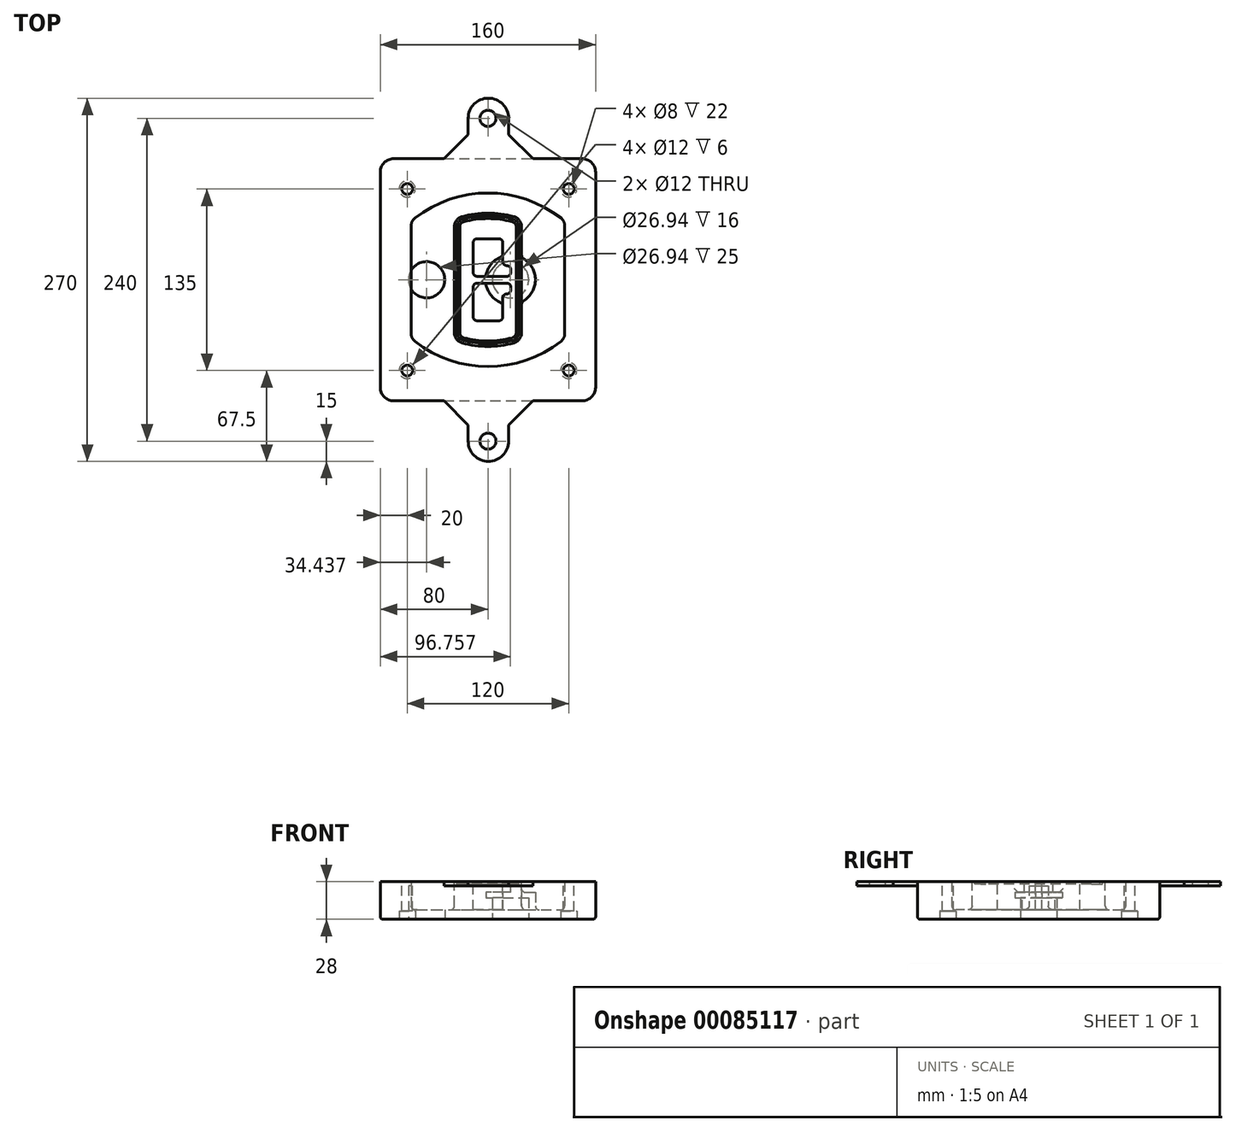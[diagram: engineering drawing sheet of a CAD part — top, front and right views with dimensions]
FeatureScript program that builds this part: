
annotation { "Feature Type Name" : "Feature", "Feature Type Description" : "" }
export const myFeature = defineFeature(function(context is Context, id is Id, definition is map)
    precondition{}
    {
        {
            var Q0;
            Q0=qCreatedBy(makeId("Top.planeOp"),FACE);
            var sketch = newSketch(context, id + "F0", { "sketchPlane" : qUnion([Q0])});
            skPoint(sketch, "E0.rect.middle", {"position": v(0, 0) * mm});
            skLineSegment(sketch, "E1.bottom", {"start": v(-70, -90) * mm, "end": v(70, -90) * mm});
            skLineSegment(sketch, "E1.top", {"start": v(-70, 90) * mm, "end": v(70, 90) * mm});
            skLineSegment(sketch, "E1.left", {"start": v(-80, -80) * mm, "end": v(-80, 80) * mm});
            skLineSegment(sketch, "E1.right", {"start": v(80, -80) * mm, "end": v(80, 80) * mm});
            skLineSegment(sketch, "E2", {"start": v(-80, 90) * mm, "end": v(80, -90) * mm, "construction": true});
            skLineSegment(sketch, "E3", {"start": v(80, 90) * mm, "end": v(-80, -90) * mm, "construction": true});
            skCircle(sketch, "E4", {"center": v(-60, 67.5) * mm, "radius": 4 * mm});
            skCircle(sketch, "E5", {"center": v(60, 67.5) * mm, "radius": 4 * mm});
            skCircle(sketch, "E6", {"center": v(60, -67.5) * mm, "radius": 4 * mm});
            skCircle(sketch, "E7", {"center": v(-60, -67.5) * mm, "radius": 4 * mm});
            skLineSegment(sketch, "E8", {"start": v(-60, 67.5) * mm, "end": v(60, 67.5) * mm, "construction": true});
            skLineSegment(sketch, "E9", {"start": v(60, 67.5) * mm, "end": v(60, -67.5) * mm, "construction": true});
            skLineSegment(sketch, "E10", {"start": v(60, -67.5) * mm, "end": v(-60, -67.5) * mm, "construction": true});
            skLineSegment(sketch, "E11", {"start": v(-60, -67.5) * mm, "end": v(-60, 67.5) * mm, "construction": true});
            skLineSegment(sketch, "E12", {"start": v(-60, 40.3) * mm, "end": v(-60, -40.3) * mm});
            skLineSegment(sketch, "E13", {"start": v(60, 40.3) * mm, "end": v(60, -40.3) * mm});
            skArc(sketch, "E14", {"start": v(56.15, 48.18) * mm, "mid": v(0, 67.5) * mm, "end": v(-56.15, 48.18) * mm});
            skArc(sketch, "E15", {"start": v(-56.15, -48.18) * mm, "mid": v(0, -67.5) * mm, "end": v(56.15, -48.18) * mm});
            skLineSegment(sketch, "E16", {"start": v(-60, 0) * mm, "end": v(60, 0) * mm, "construction": true});
            skPoint(sketch, "E17.visualSharp", {"position": v(-60, -45) * mm});
            skArc(sketch, "E17.filletArc", {"start": v(-60, -40.3) * mm, "mid": v(-58.99, -44.68) * mm, "end": v(-56.15, -48.18) * mm});
            skPoint(sketch, "E18.visualSharp", {"position": v(-60, 45) * mm});
            skArc(sketch, "E18.filletArc", {"start": v(-56.15, 48.18) * mm, "mid": v(-58.99, 44.68) * mm, "end": v(-60, 40.3) * mm});
            skPoint(sketch, "E19.visualSharp", {"position": v(60, 45) * mm});
            skArc(sketch, "E19.filletArc", {"start": v(60, 40.3) * mm, "mid": v(58.99, 44.68) * mm, "end": v(56.15, 48.18) * mm});
            skPoint(sketch, "E20.visualSharp", {"position": v(60, -45) * mm});
            skArc(sketch, "E20.filletArc", {"start": v(56.15, -48.18) * mm, "mid": v(58.99, -44.68) * mm, "end": v(60, -40.3) * mm});
            skPoint(sketch, "E21.visualSharp", {"position": v(-80, 90) * mm});
            skArc(sketch, "E21.filletArc", {"start": v(-70, 90) * mm, "mid": v(-77.07, 87.07) * mm, "end": v(-80, 80) * mm});
            skPoint(sketch, "E22.visualSharp", {"position": v(80, 90) * mm});
            skArc(sketch, "E22.filletArc", {"start": v(80, 80) * mm, "mid": v(77.07, 87.07) * mm, "end": v(70, 90) * mm});
            skPoint(sketch, "E23.visualSharp", {"position": v(80, -90) * mm});
            skArc(sketch, "E23.filletArc", {"start": v(70, -90) * mm, "mid": v(77.07, -87.07) * mm, "end": v(80, -80) * mm});
            skPoint(sketch, "E24.visualSharp", {"position": v(-80, -90) * mm});
            skArc(sketch, "E24.filletArc", {"start": v(-80, -80) * mm, "mid": v(-77.07, -87.07) * mm, "end": v(-70, -90) * mm});
            skArc(sketch, "E25.0", {"start": v(57, 40.3) * mm, "mid": v(56.3, 43.36) * mm, "end": v(54.3, 45.81) * mm});
            skLineSegment(sketch, "E25.1", {"start": v(57, 40.3) * mm, "end": v(57, -40.3) * mm});
            skArc(sketch, "E25.2", {"start": v(54.3, -45.81) * mm, "mid": v(56.3, -43.36) * mm, "end": v(57, -40.3) * mm});
            skArc(sketch, "E25.3", {"start": v(-54.3, -45.81) * mm, "mid": v(0, -64.5) * mm, "end": v(54.3, -45.81) * mm});
            skArc(sketch, "E25.4", {"start": v(-57, -40.3) * mm, "mid": v(-56.3, -43.36) * mm, "end": v(-54.3, -45.81) * mm});
            skArc(sketch, "E25.5", {"start": v(54.3, 45.81) * mm, "mid": v(0, 64.5) * mm, "end": v(-54.3, 45.81) * mm});
            skLineSegment(sketch, "E25.6", {"start": v(-57, 40.3) * mm, "end": v(-57, -40.3) * mm});
            skArc(sketch, "E25.7", {"start": v(-54.3, 45.81) * mm, "mid": v(-56.3, 43.36) * mm, "end": v(-57, 40.3) * mm});
            skArc(sketch, "E26.0", {"start": v(-58.62, 51.33) * mm, "mid": v(-62.58, 46.43) * mm, "end": v(-64, 40.3) * mm});
            skArc(sketch, "E26.1", {"start": v(58.62, 51.33) * mm, "mid": v(0, 71.5) * mm, "end": v(-58.62, 51.33) * mm});
            skArc(sketch, "E26.2", {"start": v(64, 40.3) * mm, "mid": v(62.58, 46.43) * mm, "end": v(58.62, 51.33) * mm});
            skLineSegment(sketch, "E26.3", {"start": v(64, 40.3) * mm, "end": v(64, -40.3) * mm});
            skArc(sketch, "E26.4", {"start": v(58.62, -51.33) * mm, "mid": v(62.58, -46.43) * mm, "end": v(64, -40.3) * mm});
            skLineSegment(sketch, "E26.5", {"start": v(-64, 40.3) * mm, "end": v(-64, -40.3) * mm});
            skArc(sketch, "E26.6", {"start": v(-58.62, -51.33) * mm, "mid": v(0, -71.5) * mm, "end": v(58.62, -51.33) * mm});
            skArc(sketch, "E26.7", {"start": v(-64, -40.3) * mm, "mid": v(-62.58, -46.43) * mm, "end": v(-58.62, -51.33) * mm});
            skSolve(sketch);
        }
        {
            var Q0;
            Q0=makeQuery(id+"F0.imprint","IMPRINT",FACE,{"disambiguationData":[TD([[makeQuery(id+"F0.imprint","IMPRINT",EDGE,{"derivedFrom":sQuery(id+"F0.wireOp",EDGE,"E1.bottom")}),1.0]])]});
            var Q1;
            Q1=makeQuery(id+"F0.imprint","IMPRINT",FACE,{"disambiguationData":[TD([[makeQuery(id+"F0.imprint","IMPRINT",EDGE,{"derivedFrom":sQuery(id+"F0.wireOp",EDGE,"E12")}),1.0]])]});
            var Q2;
            Q2=makeQuery(id+"F0.imprint","IMPRINT",FACE,{"disambiguationData":[TD([[makeQuery(id+"F0.imprint","IMPRINT",EDGE,{"derivedFrom":sQuery(id+"F0.wireOp",EDGE,"E25.0")}),1.0]])]});
            var Q3;
            Q3=makeQuery(id+"F0.imprint","IMPRINT",FACE,{"disambiguationData":[TD([[makeQuery(id+"F0.imprint","IMPRINT",EDGE,{"derivedFrom":sQuery(id+"F0.wireOp",EDGE,"E12")}),-1.0]])]});
            extrude(context, id + "F1", {"entities" : qUnion([Q0, Q1, Q2, Q3]), "oppositeDirection" : true, "depth" : 25 * mm});
        }
        {
            var Q0;
            Q0=makeQuery(id+"F0.imprint","IMPRINT",FACE,{"disambiguationData":[TD([[makeQuery(id+"F0.imprint","IMPRINT",EDGE,{"derivedFrom":sQuery(id+"F0.wireOp",EDGE,"E12")}),1.0]])]});
            extrude(context, id + "F2", {"entities" : qUnion([Q0]), "operationType" : NewBodyOperationType.ADD, "depth" : 3 * mm});
        }
        {
            var Q0;
            Q0=makeQuery(id+"F0.imprint","IMPRINT",FACE,{"disambiguationData":[TD([[makeQuery(id+"F0.imprint","IMPRINT",EDGE,{"derivedFrom":sQuery(id+"F0.wireOp",EDGE,"E25.0")}),1.0]])]});
            extrude(context, id + "F3", {"entities" : qUnion([Q0]), "operationType" : NewBodyOperationType.REMOVE, "oppositeDirection" : true, "depth" : 18 * mm});
        }
        {
            var Q0;
            Q0=makeQuery(id+"F2.opExtrude","CAP_FACE",FACE,{"disambiguationData":[OSD([sQuery(id+"F0.wireOp",EDGE,"E12"),sQuery(id+"F0.wireOp",EDGE,"E13"),sQuery(id+"F0.wireOp",EDGE,"E14"),sQuery(id+"F0.wireOp",EDGE,"E15"),sQuery(id+"F0.wireOp",EDGE,"E17.filletArc"),sQuery(id+"F0.wireOp",EDGE,"E18.filletArc"),sQuery(id+"F0.wireOp",EDGE,"E19.filletArc"),sQuery(id+"F0.wireOp",EDGE,"E20.filletArc"),sQuery(id+"F0.wireOp",EDGE,"E25.0"),sQuery(id+"F0.wireOp",EDGE,"E25.1"),sQuery(id+"F0.wireOp",EDGE,"E25.2"),sQuery(id+"F0.wireOp",EDGE,"E25.3"),sQuery(id+"F0.wireOp",EDGE,"E25.4"),sQuery(id+"F0.wireOp",EDGE,"E25.5"),sQuery(id+"F0.wireOp",EDGE,"E25.6"),sQuery(id+"F0.wireOp",EDGE,"E25.7")])],"isStart":false});
            var sketch = newSketch(context, id + "F4", { "sketchPlane" : qUnion([Q0])});
            skArc(sketch, "E27.0", {"start": v(-19.08, -46.97) * mm, "mid": v(0, -49.5) * mm, "end": v(19.08, -46.97) * mm});
            skArc(sketch, "E28.0", {"start": v(19.08, 46.97) * mm, "mid": v(0, 49.5) * mm, "end": v(-19.08, 46.97) * mm});
            skLineSegment(sketch, "E29", {"start": v(-25, 39.25) * mm, "end": v(-25, -39.25) * mm});
            skLineSegment(sketch, "E30", {"start": v(25, 39.25) * mm, "end": v(25, -39.25) * mm});
            skLineSegment(sketch, "E31", {"start": v(-25, 45.1) * mm, "end": v(25, 45.1) * mm, "construction": true});
            skLineSegment(sketch, "E32", {"start": v(-25, -45.1) * mm, "end": v(25, -45.1) * mm, "construction": true});
            skPoint(sketch, "E33.visualSharp", {"position": v(-25, 45.1) * mm});
            skArc(sketch, "E33.filletArc", {"start": v(-19.08, 46.97) * mm, "mid": v(-23.35, 44.11) * mm, "end": v(-25, 39.25) * mm});
            skPoint(sketch, "E34.visualSharp", {"position": v(25, 45.1) * mm});
            skArc(sketch, "E34.filletArc", {"start": v(25, 39.25) * mm, "mid": v(23.35, 44.11) * mm, "end": v(19.08, 46.97) * mm});
            skPoint(sketch, "E35.visualSharp", {"position": v(25, -45.1) * mm});
            skArc(sketch, "E35.filletArc", {"start": v(19.08, -46.97) * mm, "mid": v(23.35, -44.11) * mm, "end": v(25, -39.25) * mm});
            skPoint(sketch, "E36.visualSharp", {"position": v(-25, -45.1) * mm});
            skArc(sketch, "E36.filletArc", {"start": v(-25, -39.25) * mm, "mid": v(-23.35, -44.11) * mm, "end": v(-19.08, -46.97) * mm});
            skArc(sketch, "E37.0", {"start": v(54.3, 45.81) * mm, "mid": v(0, 64.5) * mm, "end": v(-54.3, 45.81) * mm});
            skArc(sketch, "E37.1", {"start": v(-54.3, 45.81) * mm, "mid": v(-56.3, 43.36) * mm, "end": v(-57, 40.3) * mm});
            skLineSegment(sketch, "E37.2", {"start": v(-57, 40.3) * mm, "end": v(-57, -40.3) * mm});
            skArc(sketch, "E37.3", {"start": v(-57, -40.3) * mm, "mid": v(-56.3, -43.36) * mm, "end": v(-54.3, -45.81) * mm});
            skArc(sketch, "E37.4", {"start": v(-54.3, -45.81) * mm, "mid": v(0, -64.5) * mm, "end": v(54.3, -45.81) * mm});
            skArc(sketch, "E37.5", {"start": v(54.3, -45.81) * mm, "mid": v(56.3, -43.36) * mm, "end": v(57, -40.3) * mm});
            skLineSegment(sketch, "E37.6", {"start": v(57, 40.3) * mm, "end": v(57, -40.3) * mm});
            skArc(sketch, "E37.7", {"start": v(57, 40.3) * mm, "mid": v(56.3, 43.36) * mm, "end": v(54.3, 45.81) * mm});
            skLineSegment(sketch, "E38.0", {"start": v(23, 39.25) * mm, "end": v(23, -39.25) * mm});
            skArc(sketch, "E38.1", {"start": v(18.56, -45.04) * mm, "mid": v(21.76, -42.9) * mm, "end": v(23, -39.25) * mm});
            skArc(sketch, "E38.2", {"start": v(-18.56, -45.04) * mm, "mid": v(0, -47.5) * mm, "end": v(18.56, -45.04) * mm});
            skArc(sketch, "E38.3", {"start": v(-23, -39.25) * mm, "mid": v(-21.76, -42.9) * mm, "end": v(-18.56, -45.04) * mm});
            skLineSegment(sketch, "E38.4", {"start": v(-23, 39.25) * mm, "end": v(-23, -39.25) * mm});
            skArc(sketch, "E38.5", {"start": v(23, 39.25) * mm, "mid": v(21.76, 42.9) * mm, "end": v(18.56, 45.04) * mm});
            skArc(sketch, "E38.6", {"start": v(-18.56, 45.04) * mm, "mid": v(-21.76, 42.9) * mm, "end": v(-23, 39.25) * mm});
            skArc(sketch, "E38.7", {"start": v(18.56, 45.04) * mm, "mid": v(0, 47.5) * mm, "end": v(-18.56, 45.04) * mm});
            skArc(sketch, "E39.0", {"start": v(21, 39.25) * mm, "mid": v(20.18, 41.68) * mm, "end": v(18.04, 43.1) * mm});
            skLineSegment(sketch, "E39.1", {"start": v(21, 39.25) * mm, "end": v(21, -39.25) * mm});
            skArc(sketch, "E39.2", {"start": v(18.04, -43.1) * mm, "mid": v(20.18, -41.68) * mm, "end": v(21, -39.25) * mm});
            skArc(sketch, "E39.3", {"start": v(-18.04, -43.1) * mm, "mid": v(0, -45.5) * mm, "end": v(18.04, -43.1) * mm});
            skArc(sketch, "E39.4", {"start": v(-21, -39.25) * mm, "mid": v(-20.18, -41.68) * mm, "end": v(-18.04, -43.1) * mm});
            skArc(sketch, "E39.5", {"start": v(18.04, 43.1) * mm, "mid": v(0, 45.5) * mm, "end": v(-18.04, 43.1) * mm});
            skLineSegment(sketch, "E39.6", {"start": v(-21, 39.25) * mm, "end": v(-21, -39.25) * mm});
            skArc(sketch, "E39.7", {"start": v(-18.04, 43.1) * mm, "mid": v(-20.18, 41.68) * mm, "end": v(-21, 39.25) * mm});
            skLineSegment(sketch, "E40", {"start": v(-25, 0) * mm, "end": v(25, 0) * mm, "construction": true});
            skLineSegment(sketch, "E41", {"start": v(-11, 5.5) * mm, "end": v(-11, 27.5) * mm});
            skLineSegment(sketch, "E42", {"start": v(-8, 30.5) * mm, "end": v(8, 30.5) * mm});
            skLineSegment(sketch, "E43", {"start": v(11, 27.5) * mm, "end": v(11, 13.5) * mm});
            skLineSegment(sketch, "E44", {"start": v(14, 10.5) * mm, "end": v(14, 10.5) * mm});
            skLineSegment(sketch, "E45", {"start": v(17, 7.5) * mm, "end": v(17, 5.5) * mm});
            skLineSegment(sketch, "E46", {"start": v(14, 2.5) * mm, "end": v(-8, 2.5) * mm});
            skPoint(sketch, "E47.visualSharp", {"position": v(-11, 30.5) * mm});
            skArc(sketch, "E47.filletArc", {"start": v(-8, 30.5) * mm, "mid": v(-10.12, 29.62) * mm, "end": v(-11, 27.5) * mm});
            skPoint(sketch, "E48.visualSharp", {"position": v(11, 30.5) * mm});
            skArc(sketch, "E48.filletArc", {"start": v(11, 27.5) * mm, "mid": v(10.12, 29.62) * mm, "end": v(8, 30.5) * mm});
            skPoint(sketch, "E49.visualSharp", {"position": v(11, 10.5) * mm});
            skArc(sketch, "E49.filletArc", {"start": v(11, 13.5) * mm, "mid": v(11.88, 11.38) * mm, "end": v(14, 10.5) * mm});
            skPoint(sketch, "E50.visualSharp", {"position": v(17, 10.5) * mm});
            skArc(sketch, "E50.filletArc", {"start": v(17, 7.5) * mm, "mid": v(16.12, 9.62) * mm, "end": v(14, 10.5) * mm});
            skPoint(sketch, "E51.visualSharp", {"position": v(17, 2.5) * mm});
            skArc(sketch, "E51.filletArc", {"start": v(14, 2.5) * mm, "mid": v(16.12, 3.38) * mm, "end": v(17, 5.5) * mm});
            skPoint(sketch, "E52.visualSharp", {"position": v(-11, 2.5) * mm});
            skArc(sketch, "E52.filletArc", {"start": v(-11, 5.5) * mm, "mid": v(-10.12, 3.38) * mm, "end": v(-8, 2.5) * mm});
            skLineSegment(sketch, "E53.0.MirrorCS", {"start": v(14, -2.5) * mm, "end": v(-8, -2.5) * mm});
            skArc(sketch, "E54.0.MirrorCS", {"start": v(-11, -5.5) * mm, "mid": v(-10.12, -3.38) * mm, "end": v(-8, -2.5) * mm});
            skLineSegment(sketch, "E55.0.MirrorCS", {"start": v(-11, -5.5) * mm, "end": v(-11, -27.5) * mm});
            skArc(sketch, "E56.0.MirrorCS", {"start": v(-8, -30.5) * mm, "mid": v(-10.12, -29.62) * mm, "end": v(-11, -27.5) * mm});
            skLineSegment(sketch, "E57.0.MirrorCS", {"start": v(-8, -30.5) * mm, "end": v(8, -30.5) * mm});
            skArc(sketch, "E58.0.MirrorCS", {"start": v(11, -27.5) * mm, "mid": v(10.12, -29.62) * mm, "end": v(8, -30.5) * mm});
            skLineSegment(sketch, "E59.0.MirrorCS", {"start": v(11, -27.5) * mm, "end": v(11, -13.5) * mm});
            skArc(sketch, "E60.0.MirrorCS", {"start": v(11, -13.5) * mm, "mid": v(11.88, -11.38) * mm, "end": v(14, -10.5) * mm});
            skArc(sketch, "E61.0.MirrorCS", {"start": v(17, -7.5) * mm, "mid": v(16.12, -9.62) * mm, "end": v(14, -10.5) * mm});
            skLineSegment(sketch, "E62.0.MirrorCS", {"start": v(17, -7.5) * mm, "end": v(17, -5.5) * mm});
            skArc(sketch, "E63.0.MirrorCS", {"start": v(14, -2.5) * mm, "mid": v(16.12, -3.38) * mm, "end": v(17, -5.5) * mm});
            skSolve(sketch);
        }
        {
            var Q0;
            Q0=makeQuery(id+"F4.imprint","IMPRINT",FACE,{"disambiguationData":[TD([[makeQuery(id+"F4.imprint","IMPRINT",EDGE,{"derivedFrom":sQuery(id+"F4.wireOp",EDGE,"E27.0")}),1.0]])]});
            var Q1;
            Q1=makeQuery(id+"F4.imprint","IMPRINT",FACE,{"disambiguationData":[TD([[makeQuery(id+"F4.imprint","IMPRINT",EDGE,{"derivedFrom":sQuery(id+"F4.wireOp",EDGE,"E38.0")}),-1.0]])]});
            var Q2;
            Q2=makeQuery(id+"F4.imprint","IMPRINT",FACE,{"disambiguationData":[TD([[makeQuery(id+"F4.imprint","IMPRINT",EDGE,{"derivedFrom":sQuery(id+"F4.wireOp",EDGE,"E39.0")}),1.0]])]});
            extrude(context, id + "F5", {"entities" : qUnion([Q0, Q1, Q2]), "operationType" : NewBodyOperationType.ADD, "endBound" : BoundingType.UP_TO_NEXT, "oppositeDirection" : true, "depth" : 25 * mm});
        }
        {
            var Q0;
            Q0=makeQuery(id+"F4.imprint","IMPRINT",FACE,{"disambiguationData":[TD([[makeQuery(id+"F4.imprint","IMPRINT",EDGE,{"derivedFrom":sQuery(id+"F4.wireOp",EDGE,"E38.0")}),-1.0]])]});
            extrude(context, id + "F6", {"entities" : qUnion([Q0]), "operationType" : NewBodyOperationType.REMOVE, "oppositeDirection" : true, "depth" : 2 * mm});
        }
        {
            var Q0;
            Q0=makeQuery(id+"F1.opExtrude","CAP_FACE",FACE,{"disambiguationData":[OSD([sQuery(id+"F0.wireOp",EDGE,"E1.bottom"),sQuery(id+"F0.wireOp",EDGE,"E1.top"),sQuery(id+"F0.wireOp",EDGE,"E1.left"),sQuery(id+"F0.wireOp",EDGE,"E1.right"),sQuery(id+"F0.wireOp",EDGE,"E4"),sQuery(id+"F0.wireOp",EDGE,"E5"),sQuery(id+"F0.wireOp",EDGE,"E6"),sQuery(id+"F0.wireOp",EDGE,"E7"),sQuery(id+"F0.wireOp",EDGE,"E21.filletArc"),sQuery(id+"F0.wireOp",EDGE,"E22.filletArc"),sQuery(id+"F0.wireOp",EDGE,"E23.filletArc"),sQuery(id+"F0.wireOp",EDGE,"E24.filletArc")])],"isStart":false});
            var sketch = newSketch(context, id + "F7", { "sketchPlane" : qUnion([Q0])});
            skCircle(sketch, "E64", {"center": v(16.76, 0) * mm, "radius": 13.47 * mm});
            skCircle(sketch, "E65", {"center": v(-45.56, 0) * mm, "radius": 13.47 * mm});
            skLineSegment(sketch, "E66", {"start": v(80, 0) * mm, "end": v(-80, 0) * mm});
            skCircle(sketch, "E67", {"center": v(16.76, 0) * mm, "radius": 18.47 * mm});
            skCircle(sketch, "E68", {"center": v(60, -67.5) * mm, "radius": 6 * mm});
            skCircle(sketch, "E69", {"center": v(-60, -67.5) * mm, "radius": 6 * mm});
            skCircle(sketch, "E70", {"center": v(-60, 67.5) * mm, "radius": 6 * mm});
            skCircle(sketch, "E71", {"center": v(60, 67.5) * mm, "radius": 6 * mm});
            skSolve(sketch);
        }
        {
            var Q0;
            {var subQ1=sQuery(id+"F7.wireOp",EDGE,"E66");var subQ4=sQuery(id+"F7.wireOp",EDGE,"E64");var subQ6=makeQuery(id+"F7.imprint","INTERSECT",VERTEX,{"disambiguationData":[OD(0.0)],"derivedFrom":[subQ4,subQ1]});Q0=makeQuery(id+"F7.imprint","IMPRINT",FACE,{"disambiguationData":[TD([[makeQuery(id+"F7.imprint","IMPRINT",EDGE,{"disambiguationData":[TD([[subQ6,-1.0]])],"derivedFrom":subQ4}),-1.0]])]});}
            var Q1;
            {var subQ0=sQuery(id+"F7.wireOp",EDGE,"E66");var subQ1=sQuery(id+"F7.wireOp",EDGE,"E64");var subQ3=makeQuery(id+"F7.imprint","INTERSECT",VERTEX,{"disambiguationData":[OD(0.0)],"derivedFrom":[subQ1,subQ0]});Q1=makeQuery(id+"F7.imprint","IMPRINT",FACE,{"disambiguationData":[TD([[makeQuery(id+"F7.imprint","IMPRINT",EDGE,{"disambiguationData":[TD([[subQ3,-1.0]])],"derivedFrom":subQ1}),1.0]])]});}
            var Q2;
            {var subQ0=sQuery(id+"F7.wireOp",EDGE,"E66");var subQ1=sQuery(id+"F7.wireOp",EDGE,"E64");var subQ3=makeQuery(id+"F7.imprint","INTERSECT",VERTEX,{"disambiguationData":[OD(0.0)],"derivedFrom":[subQ1,subQ0]});Q2=makeQuery(id+"F7.imprint","IMPRINT",FACE,{"disambiguationData":[TD([[makeQuery(id+"F7.imprint","IMPRINT",EDGE,{"disambiguationData":[TD([[subQ3,1.0]])],"derivedFrom":subQ1}),1.0]])]});}
            var Q3;
            {var subQ1=sQuery(id+"F7.wireOp",EDGE,"E66");var subQ4=sQuery(id+"F7.wireOp",EDGE,"E64");var subQ6=makeQuery(id+"F7.imprint","INTERSECT",VERTEX,{"disambiguationData":[OD(0.0)],"derivedFrom":[subQ4,subQ1]});Q3=makeQuery(id+"F7.imprint","IMPRINT",FACE,{"disambiguationData":[TD([[makeQuery(id+"F7.imprint","IMPRINT",EDGE,{"disambiguationData":[TD([[subQ6,1.0]])],"derivedFrom":subQ4}),-1.0]])]});}
            extrude(context, id + "F8", {"entities" : qUnion([Q0, Q1, Q2, Q3]), "operationType" : NewBodyOperationType.ADD, "oppositeDirection" : true, "depth" : 20 * mm});
        }
        {
            var Q0;
            {var subQ0=sQuery(id+"F7.wireOp",EDGE,"E66");var subQ1=sQuery(id+"F7.wireOp",EDGE,"E64");var subQ3=makeQuery(id+"F7.imprint","INTERSECT",VERTEX,{"disambiguationData":[OD(0.0)],"derivedFrom":[subQ1,subQ0]});Q0=makeQuery(id+"F7.imprint","IMPRINT",FACE,{"disambiguationData":[TD([[makeQuery(id+"F7.imprint","IMPRINT",EDGE,{"disambiguationData":[TD([[subQ3,-1.0]])],"derivedFrom":subQ1}),1.0]])]});}
            var Q1;
            {var subQ0=sQuery(id+"F7.wireOp",EDGE,"E66");var subQ1=sQuery(id+"F7.wireOp",EDGE,"E64");var subQ3=makeQuery(id+"F7.imprint","INTERSECT",VERTEX,{"disambiguationData":[OD(0.0)],"derivedFrom":[subQ1,subQ0]});Q1=makeQuery(id+"F7.imprint","IMPRINT",FACE,{"disambiguationData":[TD([[makeQuery(id+"F7.imprint","IMPRINT",EDGE,{"disambiguationData":[TD([[subQ3,1.0]])],"derivedFrom":subQ1}),1.0]])]});}
            extrude(context, id + "F9", {"entities" : qUnion([Q0, Q1]), "operationType" : NewBodyOperationType.REMOVE, "oppositeDirection" : true, "depth" : 16 * mm});
        }
        {
            var Q0;
            {var subQ0=sQuery(id+"F7.wireOp",EDGE,"E66");var subQ1=sQuery(id+"F7.wireOp",EDGE,"E65");var subQ3=makeQuery(id+"F7.imprint","INTERSECT",VERTEX,{"disambiguationData":[OD(0.0)],"derivedFrom":[subQ1,subQ0]});Q0=makeQuery(id+"F7.imprint","IMPRINT",FACE,{"disambiguationData":[TD([[makeQuery(id+"F7.imprint","IMPRINT",EDGE,{"disambiguationData":[TD([[subQ3,-1.0]])],"derivedFrom":subQ1}),1.0]])]});}
            var Q1;
            {var subQ0=sQuery(id+"F7.wireOp",EDGE,"E66");var subQ1=sQuery(id+"F7.wireOp",EDGE,"E65");var subQ3=makeQuery(id+"F7.imprint","INTERSECT",VERTEX,{"disambiguationData":[OD(0.0)],"derivedFrom":[subQ1,subQ0]});Q1=makeQuery(id+"F7.imprint","IMPRINT",FACE,{"disambiguationData":[TD([[makeQuery(id+"F7.imprint","IMPRINT",EDGE,{"disambiguationData":[TD([[subQ3,1.0]])],"derivedFrom":subQ1}),1.0]])]});}
            extrude(context, id + "F10", {"entities" : qUnion([Q0, Q1]), "operationType" : NewBodyOperationType.REMOVE, "oppositeDirection" : true, "depth" : 25 * mm});
        }
        {
            var Q0;
            Q0=makeQuery(id+"F7.imprint","IMPRINT",FACE,{"disambiguationData":[TD([[makeQuery(id+"F7.imprint","IMPRINT",EDGE,{"derivedFrom":sQuery(id+"F7.wireOp",EDGE,"E68")}),1.0]])]});
            var Q1;
            Q1=makeQuery(id+"F7.imprint","IMPRINT",FACE,{"disambiguationData":[TD([[makeQuery(id+"F7.imprint","IMPRINT",EDGE,{"derivedFrom":makeQuery(id+"F1.opExtrude","CAP_EDGE",EDGE,{"disambiguationData":[OSD([sQuery(id+"F0.wireOp",EDGE,"E5")])],"isStart":false})}),-1.0]])]});
            var Q2;
            Q2=makeQuery(id+"F7.imprint","IMPRINT",FACE,{"disambiguationData":[TD([[makeQuery(id+"F7.imprint","IMPRINT",EDGE,{"derivedFrom":sQuery(id+"F7.wireOp",EDGE,"E69")}),1.0]])]});
            var Q3;
            Q3=makeQuery(id+"F7.imprint","IMPRINT",FACE,{"disambiguationData":[TD([[makeQuery(id+"F7.imprint","IMPRINT",EDGE,{"derivedFrom":makeQuery(id+"F1.opExtrude","CAP_EDGE",EDGE,{"disambiguationData":[OSD([sQuery(id+"F0.wireOp",EDGE,"E4")])],"isStart":false})}),-1.0]])]});
            var Q4;
            Q4=makeQuery(id+"F7.imprint","IMPRINT",FACE,{"disambiguationData":[TD([[makeQuery(id+"F7.imprint","IMPRINT",EDGE,{"derivedFrom":sQuery(id+"F7.wireOp",EDGE,"E70")}),1.0]])]});
            var Q5;
            Q5=makeQuery(id+"F7.imprint","IMPRINT",FACE,{"disambiguationData":[TD([[makeQuery(id+"F7.imprint","IMPRINT",EDGE,{"derivedFrom":makeQuery(id+"F1.opExtrude","CAP_EDGE",EDGE,{"disambiguationData":[OSD([sQuery(id+"F0.wireOp",EDGE,"E7")])],"isStart":false})}),-1.0]])]});
            var Q6;
            Q6=makeQuery(id+"F7.imprint","IMPRINT",FACE,{"disambiguationData":[TD([[makeQuery(id+"F7.imprint","IMPRINT",EDGE,{"derivedFrom":sQuery(id+"F7.wireOp",EDGE,"E71")}),1.0]])]});
            var Q7;
            Q7=makeQuery(id+"F7.imprint","IMPRINT",FACE,{"disambiguationData":[TD([[makeQuery(id+"F7.imprint","IMPRINT",EDGE,{"derivedFrom":makeQuery(id+"F1.opExtrude","CAP_EDGE",EDGE,{"disambiguationData":[OSD([sQuery(id+"F0.wireOp",EDGE,"E6")])],"isStart":false})}),-1.0]])]});
            extrude(context, id + "F11", {"entities" : qUnion([Q0, Q1, Q2, Q3, Q4, Q5, Q6, Q7]), "operationType" : NewBodyOperationType.REMOVE, "oppositeDirection" : true, "depth" : 6 * mm});
        }
        {
            var Q0;
            Q0=makeQuery(id+"F9.boolean.opBoolean","COPY",FACE,{"derivedFrom":makeQuery(id+"F9.opExtrude","CAP_FACE",FACE,{"disambiguationData":[OSD([sQuery(id+"F7.wireOp",EDGE,"E64")])],"isStart":false})});
            var sketch = newSketch(context, id + "F12", { "sketchPlane" : qUnion([Q0])});
            skArc(sketch, "E72.0", {"start": v(11, 17.55) * mm, "mid": v(2.57, 11.82) * mm, "end": v(-1.54, 2.5) * mm});
            skArc(sketch, "E72.1", {"start": v(-1.54, -2.5) * mm, "mid": v(2.57, -11.82) * mm, "end": v(11, -17.55) * mm});
            skLineSegment(sketch, "E73", {"start": v(-1.54, -2.5) * mm, "end": v(14, -2.5) * mm});
            skLineSegment(sketch, "E74.0", {"start": v(14, 2.5) * mm, "end": v(-1.54, 2.5) * mm});
            skArc(sketch, "E74.1", {"start": v(14, 2.5) * mm, "mid": v(16.12, 3.38) * mm, "end": v(17, 5.5) * mm});
            skLineSegment(sketch, "E74.2", {"start": v(17, 7.5) * mm, "end": v(17, 5.5) * mm});
            skArc(sketch, "E74.3", {"start": v(17, 7.5) * mm, "mid": v(16.12, 9.62) * mm, "end": v(14, 10.5) * mm});
            skArc(sketch, "E74.4", {"start": v(11, 13.5) * mm, "mid": v(11.88, 11.38) * mm, "end": v(14, 10.5) * mm});
            skLineSegment(sketch, "E74.5", {"start": v(11, 17.55) * mm, "end": v(11, 13.5) * mm});
            skLineSegment(sketch, "E74.7", {"start": v(14, -2.5) * mm, "end": v(-1.54, -2.5) * mm});
            skArc(sketch, "E74.8", {"start": v(14, -2.5) * mm, "mid": v(16.12, -3.38) * mm, "end": v(17, -5.5) * mm});
            skLineSegment(sketch, "E74.9", {"start": v(17, -7.5) * mm, "end": v(17, -5.5) * mm});
            skArc(sketch, "E74.10", {"start": v(17, -7.5) * mm, "mid": v(16.12, -9.62) * mm, "end": v(14, -10.5) * mm});
            skArc(sketch, "E74.11", {"start": v(11, -13.5) * mm, "mid": v(11.88, -11.38) * mm, "end": v(14, -10.5) * mm});
            skLineSegment(sketch, "E74.12", {"start": v(11, -17.55) * mm, "end": v(11, -13.5) * mm});
            skPoint(sketch, "E75.orphan", {"position": v(11, -27.5) * mm});
            skPoint(sketch, "E76.orphan", {"position": v(-8, -2.5) * mm});
            skPoint(sketch, "E77.orphan", {"position": v(-8, 2.5) * mm});
            skPoint(sketch, "E78.orphan", {"position": v(11, 27.5) * mm});
            skSolve(sketch);
        }
        {
            var Q0;
            {var subQ7=sQuery(id+"F12.wireOp",EDGE,"E72.0");var subQ14=sQuery(id+"F12.wireOp",EDGE,"E72.1");var subQ16=sQuery(id+"F12.wireOp",EDGE,"E74.1");var subQ18=sQuery(id+"F12.wireOp",EDGE,"E74.8");Q0=qUnion([makeQuery(id+"F12.imprint","IMPRINT",FACE,{"disambiguationData":[TD([[makeQuery(id+"F12.imprint","IMPRINT",EDGE,{"derivedFrom":subQ7}),1.0]])]}),makeQuery(id+"F12.imprint","IMPRINT",FACE,{"disambiguationData":[TD([[makeQuery(id+"F12.imprint","IMPRINT",EDGE,{"derivedFrom":subQ14}),1.0]])]}),makeQuery(id+"F12.imprint","IMPRINT",FACE,{"disambiguationData":[TD([[makeQuery(id+"F12.imprint","IMPRINT",EDGE,{"derivedFrom":subQ16}),1.0]])]}),makeQuery(id+"F12.imprint","IMPRINT",FACE,{"disambiguationData":[TD([[makeQuery(id+"F12.imprint","IMPRINT",EDGE,{"derivedFrom":subQ18}),-1.0]])]})]);}
            var Q1;
            Q1=makeQuery(id+"F5.boolean.opBoolean","SPLIT",FACE,{"disambiguationData":[TD([makeQuery(id+"F5.opExtrude","SWEPT_FACE",FACE,{"disambiguationData":[OSD([sQuery(id+"F4.wireOp",EDGE,"E41")])]})])],"derivedFrom":makeQuery(id+"F3.boolean.opBoolean","COPY",FACE,{"derivedFrom":makeQuery(id+"F3.opExtrude","CAP_FACE",FACE,{"disambiguationData":[OSD([sQuery(id+"F0.wireOp",EDGE,"E25.0"),sQuery(id+"F0.wireOp",EDGE,"E25.1"),sQuery(id+"F0.wireOp",EDGE,"E25.2"),sQuery(id+"F0.wireOp",EDGE,"E25.3"),sQuery(id+"F0.wireOp",EDGE,"E25.4"),sQuery(id+"F0.wireOp",EDGE,"E25.5"),sQuery(id+"F0.wireOp",EDGE,"E25.6"),sQuery(id+"F0.wireOp",EDGE,"E25.7")])],"isStart":false})})});
            extrude(context, id + "F13", {"entities" : qUnion([Q0]), "operationType" : NewBodyOperationType.REMOVE, "endBound" : BoundingType.UP_TO_SURFACE, "endBoundEntityFace" : qUnion([Q1]), "depth" : 25 * mm});
        }
        {
            var Q0;
            Q0=makeQuery(id+"F3.boolean.opBoolean","COPY",EDGE,{"derivedFrom":makeQuery(id+"F3.opExtrude","CAP_EDGE",EDGE,{"disambiguationData":[OSD([sQuery(id+"F0.wireOp",EDGE,"E25.6")])],"isStart":false})});
            var Q1;
            Q1=makeQuery(id+"F8.boolean.opBoolean","INTERSECT",EDGE,{"derivedFrom":[makeQuery(id+"F5.opExtrude","SWEPT_FACE",FACE,{"disambiguationData":[OSD([sQuery(id+"F4.wireOp",EDGE,"E30")])]}),makeQuery(id+"F8.opExtrude","CAP_FACE",FACE,{"disambiguationData":[OSD([sQuery(id+"F7.wireOp",EDGE,"E67")])],"isStart":false})]});
            var Q2;
            Q2=makeQuery(id+"F8.boolean.opBoolean","INTERSECT",EDGE,{"disambiguationData":[OD(1.0)],"derivedFrom":[makeQuery(id+"F5.opExtrude","SWEPT_FACE",FACE,{"disambiguationData":[OSD([sQuery(id+"F4.wireOp",EDGE,"E30")])]}),makeQuery(id+"F8.opExtrude","SWEPT_FACE",FACE,{"disambiguationData":[OSD([sQuery(id+"F7.wireOp",EDGE,"E67")])]})]});
            var Q3;
            {var subQ0=sQuery(id+"F4.wireOp",EDGE,"E30");Q3=makeQuery(id+"F8.boolean.opBoolean","SPLIT",EDGE,{"disambiguationData":[TD([makeQuery(id+"F5.opExtrude","SWEPT_FACE",FACE,{"disambiguationData":[OSD([sQuery(id+"F4.wireOp",EDGE,"E35.filletArc")])]})])],"derivedFrom":makeQuery(id+"F5.opExtrude","CAP_EDGE",EDGE,{"disambiguationData":[OSD([subQ0])],"isStart":false})});}
            var Q4;
            {var subQ0=sQuery(id+"F0.wireOp",EDGE,"E25.7");var subQ1=sQuery(id+"F0.wireOp",EDGE,"E25.1");var subQ2=sQuery(id+"F0.wireOp",EDGE,"E25.6");var subQ3=sQuery(id+"F0.wireOp",EDGE,"E25.5");var subQ4=sQuery(id+"F0.wireOp",EDGE,"E25.4");var subQ5=sQuery(id+"F0.wireOp",EDGE,"E25.0");var subQ6=sQuery(id+"F0.wireOp",EDGE,"E25.2");var subQ7=sQuery(id+"F0.wireOp",EDGE,"E25.3");Q4=makeQuery(id+"F8.boolean.opBoolean","INTERSECT",EDGE,{"derivedFrom":[makeQuery(id+"F5.boolean.opBoolean","SPLIT",FACE,{"disambiguationData":[TD([makeQuery(id+"F2.opExtrude","SWEPT_FACE",FACE,{"disambiguationData":[OSD([subQ5])]})])],"derivedFrom":makeQuery(id+"F3.boolean.opBoolean","COPY",FACE,{"derivedFrom":makeQuery(id+"F3.opExtrude","CAP_FACE",FACE,{"disambiguationData":[OSD([subQ5,subQ1,subQ6,subQ7,subQ4,subQ3,subQ2,subQ0])],"isStart":false})})}),makeQuery(id+"F8.opExtrude","SWEPT_FACE",FACE,{"disambiguationData":[OSD([sQuery(id+"F7.wireOp",EDGE,"E67")])]})]});}
            var Q5;
            Q5=makeQuery(id+"F8.boolean.opBoolean","INTERSECT",EDGE,{"disambiguationData":[OD(0.0)],"derivedFrom":[makeQuery(id+"F5.opExtrude","SWEPT_FACE",FACE,{"disambiguationData":[OSD([sQuery(id+"F4.wireOp",EDGE,"E30")])]}),makeQuery(id+"F8.opExtrude","SWEPT_FACE",FACE,{"disambiguationData":[OSD([sQuery(id+"F7.wireOp",EDGE,"E67")])]})]});
            fillet(context, id + "F14", {"entities" : qUnion([Q0, Q1, Q2, Q3, Q4, Q5]), "radius" : 3 * mm, "tangentPropagation" : true, "allowEdgeOverflow" : false});
        }
        {
            var Q0;
            Q0=makeQuery(id+"F1.opExtrude","CAP_EDGE",EDGE,{"disambiguationData":[OSD([sQuery(id+"F0.wireOp",EDGE,"E1.bottom")])],"isStart":false});
            fillet(context, id + "F15", {"entities" : qUnion([Q0]), "radius" : 2 * mm, "tangentPropagation" : true, "allowEdgeOverflow" : false});
        }
        {
            var Q0;
            {var subQ0=sQuery(id+"F0.wireOp",EDGE,"E22.filletArc");var subQ1=sQuery(id+"F0.wireOp",EDGE,"E7");var subQ2=sQuery(id+"F0.wireOp",EDGE,"E6");var subQ3=sQuery(id+"F0.wireOp",EDGE,"E5");var subQ4=sQuery(id+"F0.wireOp",EDGE,"E4");var subQ5=sQuery(id+"F0.wireOp",EDGE,"E1.bottom");var subQ6=sQuery(id+"F0.wireOp",EDGE,"E21.filletArc");var subQ7=sQuery(id+"F0.wireOp",EDGE,"E1.top");var subQ8=sQuery(id+"F0.wireOp",EDGE,"E1.left");var subQ9=sQuery(id+"F0.wireOp",EDGE,"E1.right");var subQ10=sQuery(id+"F0.wireOp",EDGE,"E23.filletArc");var subQ11=sQuery(id+"F0.wireOp",EDGE,"E24.filletArc");Q0=makeQuery(id+"F2.boolean.opBoolean","SPLIT",FACE,{"disambiguationData":[TD([makeQuery(id+"F1.opExtrude","SWEPT_FACE",FACE,{"disambiguationData":[OSD([subQ5])]})])],"derivedFrom":makeQuery(id+"F1.opExtrude","CAP_FACE",FACE,{"disambiguationData":[OSD([subQ5,subQ7,subQ8,subQ9,subQ4,subQ3,subQ2,subQ1,subQ6,subQ0,subQ10,subQ11])],"isStart":true})});}
            var sketch = newSketch(context, id + "F16", { "sketchPlane" : qUnion([Q0])});
            skLineSegment(sketch, "E79", {"start": v(0, 90) * mm, "end": v(0, 120) * mm, "construction": true});
            skPoint(sketch, "E79.endSnap0", {"position": v(0, 90) * mm});
            skCircle(sketch, "E80", {"center": v(0, 120) * mm, "radius": 6 * mm});
            skLineSegment(sketch, "E81", {"start": v(15.3, 120) * mm, "end": v(15.3, 108) * mm});
            skLineSegment(sketch, "E82", {"start": v(15.3, 108) * mm, "end": v(33.3, 90) * mm});
            skLineSegment(sketch, "E83", {"start": v(-14.7, 120) * mm, "end": v(-14.7, 108) * mm});
            skLineSegment(sketch, "E84", {"start": v(-14.7, 108) * mm, "end": v(-32.7, 90) * mm});
            skArc(sketch, "E85", {"start": v(15.3, 120) * mm, "mid": v(0.3, 135) * mm, "end": v(-14.7, 120) * mm});
            skLineSegment(sketch, "E86", {"start": v(-88.78, 0) * mm, "end": v(126.15, 0) * mm, "construction": true});
            skPoint(sketch, "E86.startSnap0", {"position": v(-80, 0) * mm});
            skPoint(sketch, "E86.endSnap0", {"position": v(-60, 0) * mm});
            skLineSegment(sketch, "E87.MirrorCS", {"start": v(15.3, -120) * mm, "end": v(15.3, -108) * mm});
            skPoint(sketch, "E88.MirrorP", {"position": v(0, -90) * mm});
            skCircle(sketch, "E89.MirrorC", {"center": v(0, -120) * mm, "radius": 6 * mm});
            skLineSegment(sketch, "E90.MirrorCS", {"start": v(-14.7, -120) * mm, "end": v(-14.7, -108) * mm});
            skArc(sketch, "E91.MirrorCS", {"start": v(15.3, -120) * mm, "mid": v(0.3, -135) * mm, "end": v(-14.7, -120) * mm});
            skLineSegment(sketch, "E92.MirrorCS", {"start": v(15.3, -108) * mm, "end": v(33.3, -90) * mm});
            skLineSegment(sketch, "E93.MirrorCS", {"start": v(-14.7, -108) * mm, "end": v(-32.7, -90) * mm});
            skSolve(sketch);
        }
        {
            var Q0;
            Q0=makeQuery(id+"F16.imprint","IMPRINT",FACE,{"disambiguationData":[TD([[makeQuery(id+"F16.imprint","IMPRINT",EDGE,{"derivedFrom":makeQuery(id+"F1.opExtrude","CAP_EDGE",EDGE,{"disambiguationData":[OSD([sQuery(id+"F0.wireOp",EDGE,"E1.left")])],"isStart":true})}),-1.0]])]});
            var Q1;
            Q1=makeQuery(id+"F16.imprint","IMPRINT",FACE,{"disambiguationData":[TD([[makeQuery(id+"F16.imprint","IMPRINT",EDGE,{"derivedFrom":sQuery(id+"F16.wireOp",EDGE,"E87.MirrorCS")}),1.0]])]});
            var Q2;
            Q2=makeQuery(id+"F16.imprint","IMPRINT",FACE,{"disambiguationData":[TD([[makeQuery(id+"F16.imprint","IMPRINT",EDGE,{"derivedFrom":sQuery(id+"F16.wireOp",EDGE,"E80")}),-1.0]])]});
            var Q3;
            Q3=makeQuery(id+"F2.opExtrude","CAP_FACE",FACE,{"disambiguationData":[OSD([sQuery(id+"F0.wireOp",EDGE,"E12"),sQuery(id+"F0.wireOp",EDGE,"E13"),sQuery(id+"F0.wireOp",EDGE,"E14"),sQuery(id+"F0.wireOp",EDGE,"E15"),sQuery(id+"F0.wireOp",EDGE,"E17.filletArc"),sQuery(id+"F0.wireOp",EDGE,"E18.filletArc"),sQuery(id+"F0.wireOp",EDGE,"E19.filletArc"),sQuery(id+"F0.wireOp",EDGE,"E20.filletArc"),sQuery(id+"F0.wireOp",EDGE,"E25.0"),sQuery(id+"F0.wireOp",EDGE,"E25.1"),sQuery(id+"F0.wireOp",EDGE,"E25.2"),sQuery(id+"F0.wireOp",EDGE,"E25.3"),sQuery(id+"F0.wireOp",EDGE,"E25.4"),sQuery(id+"F0.wireOp",EDGE,"E25.5"),sQuery(id+"F0.wireOp",EDGE,"E25.6"),sQuery(id+"F0.wireOp",EDGE,"E25.7")])],"isStart":false});
            extrude(context, id + "F17", {"entities" : qUnion([Q0, Q1, Q2]), "operationType" : NewBodyOperationType.ADD, "endBound" : BoundingType.UP_TO_SURFACE, "endBoundEntityFace" : qUnion([Q3]), "depth" : 25 * mm});
        }
    });
